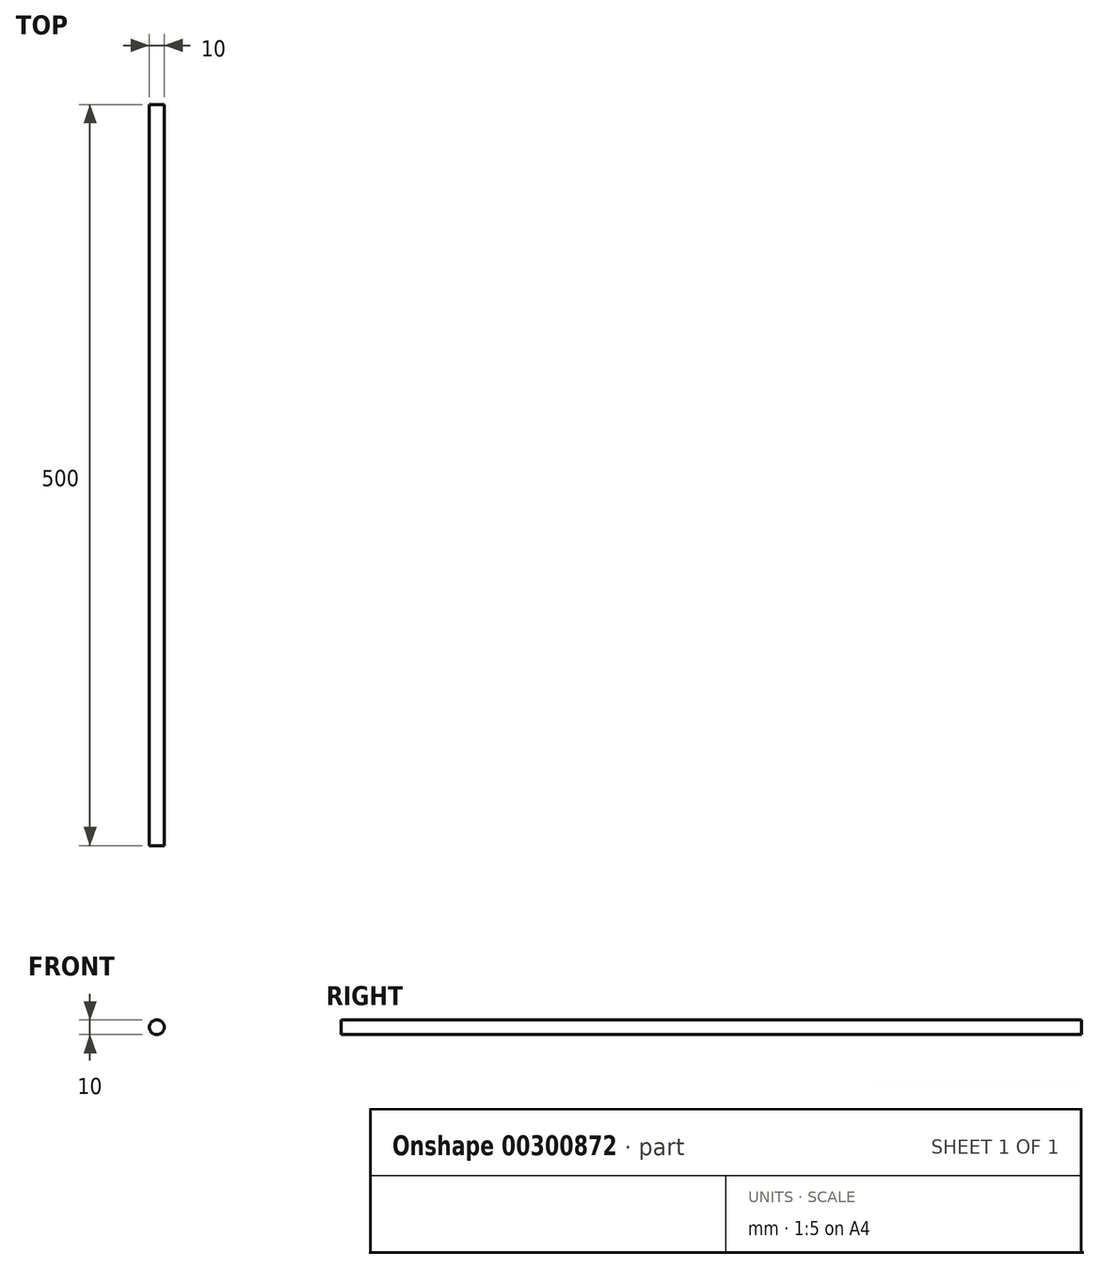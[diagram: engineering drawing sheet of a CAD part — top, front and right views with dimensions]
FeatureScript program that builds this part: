
annotation { "Feature Type Name" : "Feature", "Feature Type Description" : "" }
export const myFeature = defineFeature(function(context is Context, id is Id, definition is map)
    precondition{}
    {
        {
            var Q0;
            Q0=qCreatedBy(makeId("Front.planeOp"),FACE);
            var sketch = newSketch(context, id + "F0", { "sketchPlane" : qUnion([Q0])});
            skCircle(sketch, "E0", {"center": v(0, 0) * mm, "radius": 5 * mm});
            skSolve(sketch);
        }
        {
            var Q0;
            Q0=makeQuery(id+"F0.imprint","IMPRINT",FACE,{"disambiguationData":[TD([[makeQuery(id+"F0.imprint","IMPRINT",EDGE,{"derivedFrom":sQuery(id+"F0.wireOp",EDGE,"E0")}),1.0]])]});
            extrude(context, id + "F1", {"entities" : qUnion([Q0]), "depth" : 500 * mm});
        }
    });
